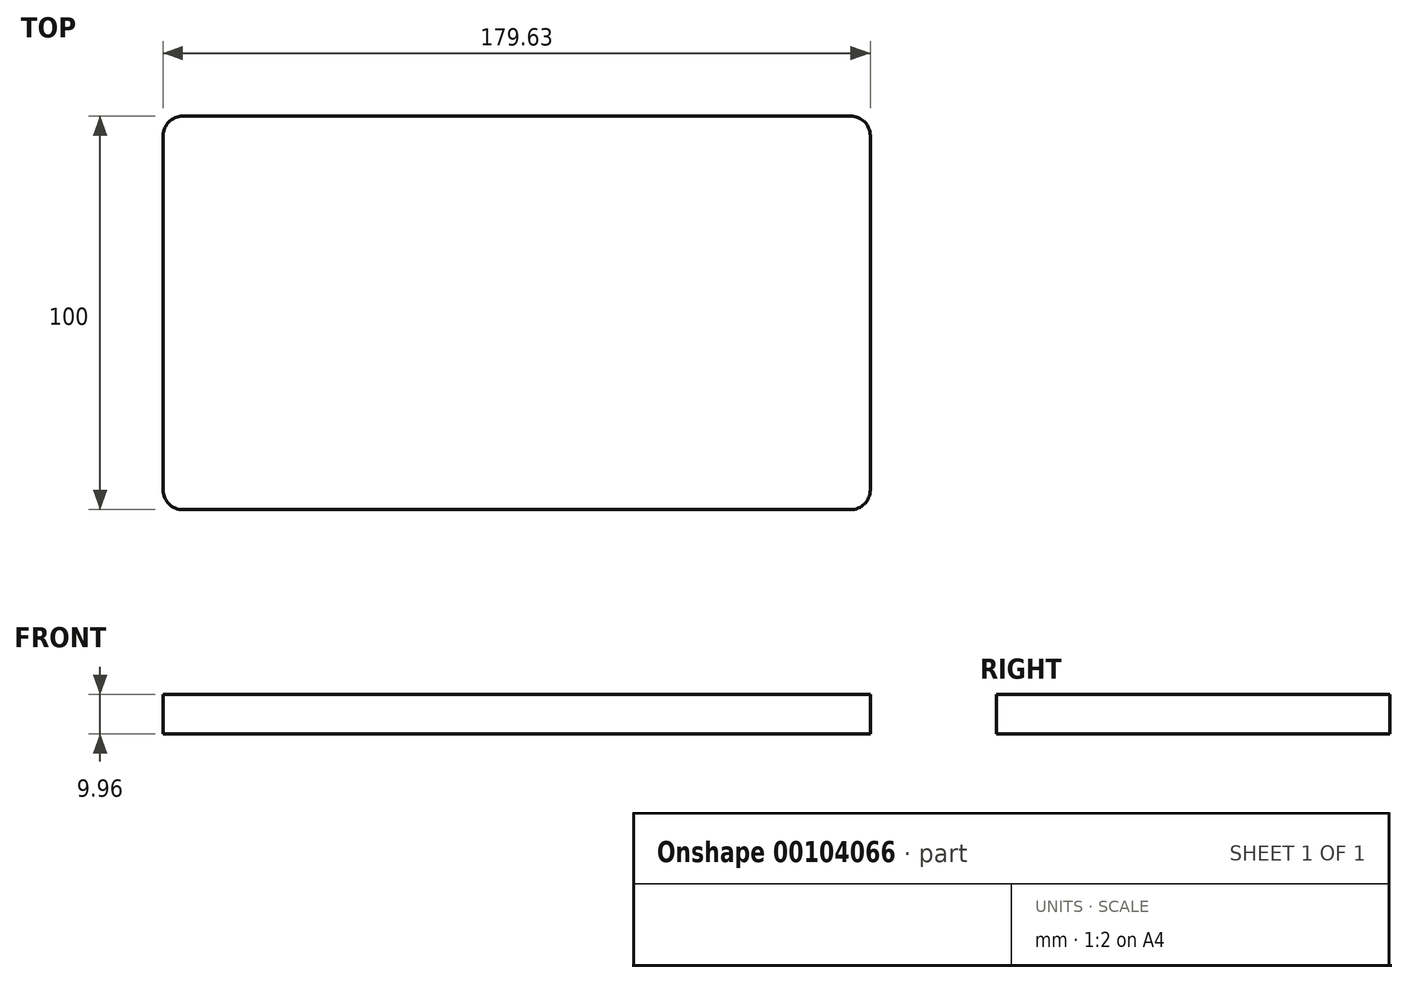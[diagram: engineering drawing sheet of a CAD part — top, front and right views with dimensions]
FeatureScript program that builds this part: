
annotation { "Feature Type Name" : "Feature", "Feature Type Description" : "" }
export const myFeature = defineFeature(function(context is Context, id is Id, definition is map)
    precondition{}
    {
        {
            var Q0;
            Q0=qCreatedBy(makeId("Front.planeOp"),FACE);
            var sketch = newSketch(context, id + "F0", { "sketchPlane" : qUnion([Q0])});
            skLineSegment(sketch, "E0.bottom", {"start": v(-119.08, 13.7) * mm, "end": v(60.55, 13.7) * mm});
            skLineSegment(sketch, "E0.top", {"start": v(-119.08, 3.74) * mm, "end": v(60.55, 3.74) * mm});
            skLineSegment(sketch, "E0.left", {"start": v(-119.08, 13.7) * mm, "end": v(-119.08, 3.74) * mm});
            skLineSegment(sketch, "E0.right", {"start": v(60.55, 13.7) * mm, "end": v(60.55, 3.74) * mm});
            skSolve(sketch);
        }
        {
            var Q0;
            Q0=makeQuery(id+"F0.imprint","IMPRINT",FACE,{"disambiguationData":[TD([[makeQuery(id+"F0.imprint","IMPRINT",EDGE,{"derivedFrom":sQuery(id+"F0.wireOp",EDGE,"E0.bottom")}),-1.0]])]});
            extrude(context, id + "F1", {"entities" : qUnion([Q0]), "endBound" : BoundingType.SYMMETRIC, "depth" : 100 * mm});
        }
        {
            var Q0;
            Q0=makeQuery(id+"F1.opExtrude","CAP_EDGE",EDGE,{"disambiguationData":[OSD([sQuery(id+"F0.wireOp",EDGE,"E0.right")])],"isStart":true});
            var Q1;
            Q1=makeQuery(id+"F1.opExtrude","CAP_EDGE",EDGE,{"disambiguationData":[OSD([sQuery(id+"F0.wireOp",EDGE,"E0.right")])],"isStart":false});
            var Q2;
            Q2=makeQuery(id+"F1.opExtrude","CAP_EDGE",EDGE,{"disambiguationData":[OSD([sQuery(id+"F0.wireOp",EDGE,"E0.left")])],"isStart":false});
            var Q3;
            Q3=makeQuery(id+"F1.opExtrude","CAP_EDGE",EDGE,{"disambiguationData":[OSD([sQuery(id+"F0.wireOp",EDGE,"E0.left")])],"isStart":true});
            fillet(context, id + "F2", {"entities" : qUnion([Q0, Q1, Q2, Q3]), "radius" : 5 * mm, "tangentPropagation" : true, "allowEdgeOverflow" : false});
        }
    });
